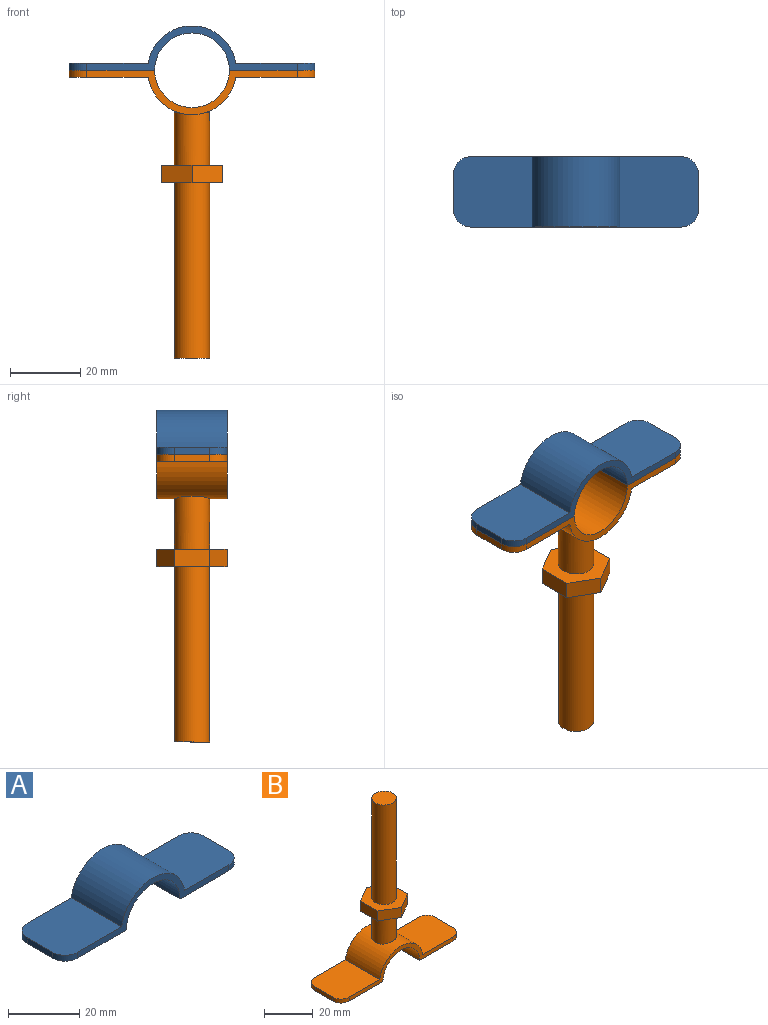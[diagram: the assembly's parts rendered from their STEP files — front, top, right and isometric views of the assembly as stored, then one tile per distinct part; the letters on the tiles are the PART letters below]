
ASSEMBLY  parts=2 mates=1
PART A: 14 faces, bbox 70x20x12.7 mm
  f0: plane 22.51x20mm, normal (0,0,1), area 439.5mm2, adj f1,f7,f8,f9,f11,f13
  f1: cylinder r=12.65mm len=24.98mm, axis (0,1,0), area 714.5mm2, adj f0,f2,f8,f9
  f2: plane 22.51x20mm, normal (0,0,1), area 439.5mm2, adj f1,f3,f8,f9,f10,f12
  f3: plane 10x2mm, normal (-1,0,0), area 20mm2, adj f2,f4,f10,f12
  f4: plane 24.35x20mm, normal (0,0,-1), area 476.3mm2, adj f3,f5,f8,f9,f10,f12
  f5: cylinder r=10.65mm len=21.3mm, axis (0,1,0), area 669.2mm2, adj f4,f6,f8,f9
  f6: plane 24.35x20mm, normal (0,0,-1), area 476.3mm2, adj f5,f7,f8,f9,f11,f13
  f7: plane 10x2mm, normal (1,0,0), area 20mm2, adj f0,f6,f11,f13
  f8: plane 60x12.65mm, normal (0,-1,0), area 142.8mm2, adj f0,f1,f2,f4,f5,f6,f12,f13
  f9: plane 60x12.65mm, normal (0,1,0), area 142.8mm2, adj f0,f1,f2,f4,f5,f6,f10,f11
  f10: cylinder r=5mm len=5mm, axis (0,0,-1), area 15.7mm2, adj f2,f3,f4,f9
  f11: cylinder r=5mm len=5mm, axis (0,0,1), area 15.7mm2, adj f0,f6,f7,f9
  f12: cylinder r=5mm len=5mm, axis (0,0,1), area 15.7mm2, adj f2,f3,f4,f8
  f13: cylinder r=5mm len=5mm, axis (0,0,-1), area 15.7mm2, adj f0,f6,f7,f8
PART B: 27 faces, bbox 70x20x82 mm
  f0: cylinder r=12.65mm len=24.98mm, axis (0,1,0), area 643mm2, adj f1,f2,f8,f9,f10,f11,f12
  f1: plane 22.51x20mm, normal (0,0,1), area 439.5mm2, adj f0,f7,f8,f9,f24,f26
  f2: plane 22.51x20mm, normal (0,0,1), area 439.5mm2, adj f0,f3,f8,f9,f23,f25
  f3: plane 10x2mm, normal (-1,0,0), area 20mm2, adj f2,f4,f23,f25
  f4: plane 24.35x20mm, normal (0,0,-1), area 476.3mm2, adj f3,f5,f8,f9,f23,f25
  f5: cylinder r=10.65mm len=21.3mm, axis (0,1,0), area 669.2mm2, adj f4,f6,f8,f9
  f6: plane 24.35x20mm, normal (0,0,-1), area 476.3mm2, adj f5,f7,f8,f9,f24,f26
  f7: plane 10x2mm, normal (1,0,0), area 20mm2, adj f1,f6,f24,f26
  f8: plane 60x12.65mm, normal (0,-1,0), area 142.8mm2, adj f0,f1,f2,f4,f5,f6,f25,f26
  f9: plane 60x12.65mm, normal (0,1,0), area 142.8mm2, adj f0,f1,f2,f4,f5,f6,f23,f24
  f10: cylinder r=5mm len=15mm, axis (0,0,-1), area 463.7mm2, adj f0,f11,f12,f20
  f11: plane 5.99x1mm, normal (0,0,-1), area 4.1mm2, adj f0,f10
  f12: plane 5.99x1mm, normal (0,0,-1), area 4.1mm2, adj f0,f10
  f13: plane 10x5mm, normal (1,0,0), area 50mm2, adj f14,f18,f19,f20
  f14: plane 8.66x5mm, normal (0.5,0.87,0), area 50mm2, adj f13,f15,f19,f20
  f15: plane 8.66x5mm, normal (-0.5,0.87,0), area 50mm2, adj f14,f16,f19,f20
  f16: plane 10x5mm, normal (-1,0,0), area 50mm2, adj f15,f17,f19,f20
  f17: plane 8.66x5mm, normal (-0.5,-0.87,0), area 50mm2, adj f16,f18,f19,f20
  f18: plane 8.66x5mm, normal (0.5,-0.87,0), area 50mm2, adj f13,f17,f19,f20
  f19: plane 20x17.32mm, normal (0,0,1), area 181.3mm2, adj f13,f14,f15,f16,f17,f18,f21
  f20: plane 20x17.32mm, normal (0,0,-1), area 181.3mm2, adj f10,f13,f14,f15,f16,f17,f18
  f21: cylinder r=5mm len=50mm, axis (0,0,-1), area 1570.8mm2, adj f19,f22
  f22: plane 10x10mm, normal (0,0,1), area 78.5mm2, adj f21
  f23: cylinder r=5mm len=5mm, axis (0,0,-1), area 15.7mm2, adj f2,f3,f4,f9
  f24: cylinder r=5mm len=5mm, axis (0,0,1), area 15.7mm2, adj f1,f6,f7,f9
  f25: cylinder r=5mm len=5mm, axis (0,0,1), area 15.7mm2, adj f2,f3,f4,f8
  f26: cylinder r=5mm len=5mm, axis (0,0,-1), area 15.7mm2, adj f1,f6,f7,f8
PLACE A t=(-20.77,9.6,-48.39)mm
PLACE B rot(axis=(-1,0,0),180deg) t=(-20.77,-10.4,-50.39)mm
MATE fastened A.f6 <-> B.f6  axis (0,0,-1) through (1.8,-0.4,-49.39)mm
